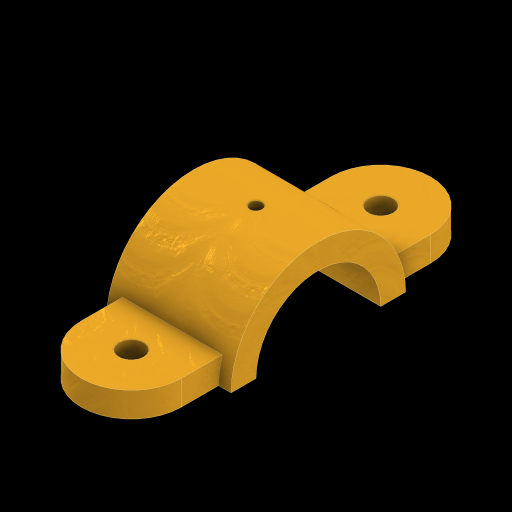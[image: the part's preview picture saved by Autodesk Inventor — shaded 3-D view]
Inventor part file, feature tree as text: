
AUTODESK INVENTOR PART (.ipt)
format: ipt  version: 2024 (Build 280153000, 153)  size: 217,088 bytes
history: native  units: in
note: dims shown in document units (in); Inventor stores cm internally (conversion verified against a paired STEP export)
features: extrude x6, sketch x5
ambient origin geometry x8: Origin, YZ Plane, XZ Plane, XY Plane, X Axis, Y Axis, Z Axis, Center Point
bodies: Solid1 (feature_tree)
feature tree (11):
  extrude  "BASE"  Depth=0.5in
  sketch  "Sketch2"  dims[d2=0.5in d3=1.0in]
  extrude  "REMOVED CENTER OF BASE"  Depth=1.0in
  extrude  "ARCH"  Depth=1.75in
  extrude  "TOPHOLE"  TaperAngle=0.0deg  [1 undecoded]
  extrude  "CIRCULAR"  Depth=1.25in
  extrude  "SQUARE"  TaperAngle=0.0deg  [1 undecoded]
  sketch  "Sketch1"  dims[d0=5.0in d1=0.5in]
  sketch  "Sketch3"  dims[d5=0.5in d6=0.0in d7=1.75in]
  sketch  "Sketch5"  dims[d8=1.25in d9=0.0in d10=0.0in]
  sketch  "Sketch6"  dims[d11=2.5in d12=0.0in d13=0.25in d14=0.0in d15=0.0in d16=2.5in d17=1.25in d18=0.625in d19=0.0in d20=0.0in d21=2.5in d22=0.0in d23=2.0in d24=1.0in d25=1.0in d26=1.25in]
note: 2 required parameter values undecoded (feature->parameter linkage not recoverable at this tier; creation-order binding heuristic only, values carry confidence <= 0.55)
